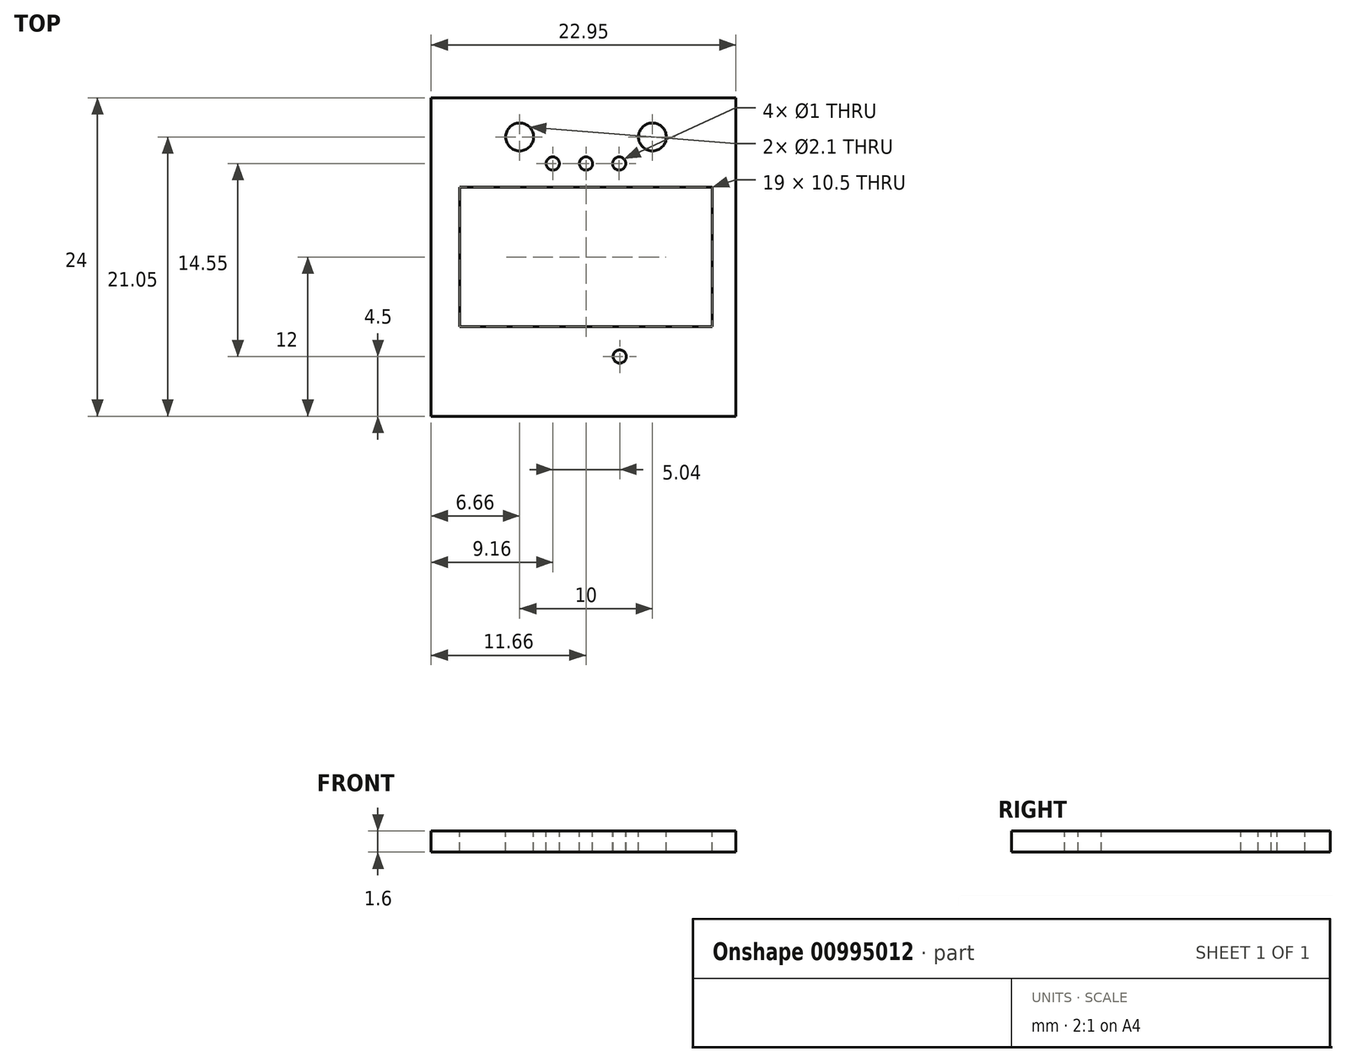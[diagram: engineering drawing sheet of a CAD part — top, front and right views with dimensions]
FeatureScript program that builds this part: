
annotation { "Feature Type Name" : "Feature", "Feature Type Description" : "" }
export const myFeature = defineFeature(function(context is Context, id is Id, definition is map)
    precondition{}
    {
        {
            var Q0;
            Q0=qCreatedBy(makeId("Top.planeOp"),FACE);
            var sketch = newSketch(context, id + "F0", { "sketchPlane" : qUnion([Q0])});
            skLineSegment(sketch, "E0.top", {"start": v(-11.66, -12) * mm, "end": v(11.3, -12) * mm});
            skLineSegment(sketch, "E0.left", {"start": v(-11.66, 12) * mm, "end": v(-11.66, -12) * mm});
            skLineSegment(sketch, "E0.right", {"start": v(11.3, 12) * mm, "end": v(11.3, -12) * mm});
            skCircle(sketch, "E1", {"center": v(0, 7.05) * mm, "radius": 0.5 * mm});
            skCircle(sketch, "E2", {"center": v(-2.5, 7.05) * mm, "radius": 0.5 * mm});
            skCircle(sketch, "E3", {"center": v(2.5, 7.05) * mm, "radius": 0.5 * mm});
            skCircle(sketch, "E4", {"center": v(2.54, -7.5) * mm, "radius": 0.5 * mm});
            skLineSegment(sketch, "E5", {"start": v(0, 0.55) * mm, "end": v(0, 1.75) * mm});
            skPoint(sketch, "E6", {"position": v(0, 6.3) * mm});
            skCircle(sketch, "E7", {"center": v(-5, 9.05) * mm, "radius": 1.05 * mm});
            skCircle(sketch, "E8", {"center": v(5, 9.05) * mm, "radius": 1.05 * mm});
            skLineSegment(sketch, "E9", {"start": v(-11.66, 12) * mm, "end": v(11.3, 12) * mm});
            skSolve(sketch);
        }
        {
            var Q0;
            Q0=qSketchRegion(id+"F0",true);
            extrude(context, id + "F1", {"entities" : qUnion([Q0]), "oppositeDirection" : true, "depth" : 1.6 * mm, "offsetDistance" : 25 * mm});
        }
        {
            var Q0;
            Q0=makeQuery(id+"F1.opExtrude","CAP_FACE",FACE,{"disambiguationData":[OSD([sQuery(id+"F0.wireOp",EDGE,"E0.bottom"),sQuery(id+"F0.wireOp",EDGE,"E0.top"),sQuery(id+"F0.wireOp",EDGE,"E0.left"),sQuery(id+"F0.wireOp",EDGE,"E0.right"),sQuery(id+"F0.wireOp",EDGE,"E1"),sQuery(id+"F0.wireOp",EDGE,"E2"),sQuery(id+"F0.wireOp",EDGE,"E3"),sQuery(id+"F0.wireOp",EDGE,"E4"),sQuery(id+"F0.wireOp",EDGE,"9yhu0ApJ-A9Rv-WkGQ-m5Oh-gTQB5OdKfF1x.bottom"),sQuery(id+"F0.wireOp",EDGE,"9yhu0ApJ-A9Rv-WkGQ-m5Oh-gTQB5OdKfF1x.top"),sQuery(id+"F0.wireOp",EDGE,"9yhu0ApJ-A9Rv-WkGQ-m5Oh-gTQB5OdKfF1x.left"),sQuery(id+"F0.wireOp",EDGE,"9yhu0ApJ-A9Rv-WkGQ-m5Oh-gTQB5OdKfF1x.right"),sQuery(id+"F0.wireOp",EDGE,"05f9d2f0-11d9-4e1b-b2fe-26b268615fe30.MirrorCS"),sQuery(id+"F0.wireOp",EDGE,"05f9d2f0-11d9-4e1b-b2fe-26b268615fe31.MirrorCS"),sQuery(id+"F0.wireOp",EDGE,"05f9d2f0-11d9-4e1b-b2fe-26b268615fe32.MirrorCS"),sQuery(id+"F0.wireOp",EDGE,"05f9d2f0-11d9-4e1b-b2fe-26b268615fe33.MirrorCS")])],"isStart":true});
            var sketch = newSketch(context, id + "F2", { "sketchPlane" : qUnion([Q0])});
            skLineSegment(sketch, "E10.bottom", {"start": v(9.5, 5.25) * mm, "end": v(-9.5, 5.25) * mm});
            skLineSegment(sketch, "E10.top", {"start": v(9.5, -5.25) * mm, "end": v(-9.5, -5.25) * mm});
            skLineSegment(sketch, "E10.left", {"start": v(9.5, 5.25) * mm, "end": v(9.5, -5.25) * mm});
            skLineSegment(sketch, "E10.right", {"start": v(-9.5, 5.25) * mm, "end": v(-9.5, -5.25) * mm});
            skPoint(sketch, "E10.middle", {"position": v(0, 0) * mm});
            skSolve(sketch);
        }
        {
            var Q0;
            Q0=qSketchRegion(id+"F2",true);
            extrude(context, id + "F3", {"entities" : qUnion([Q0]), "operationType" : NewBodyOperationType.REMOVE, "oppositeDirection" : true, "depth" : 25 * mm, "offsetDistance" : 25 * mm});
        }
    });
